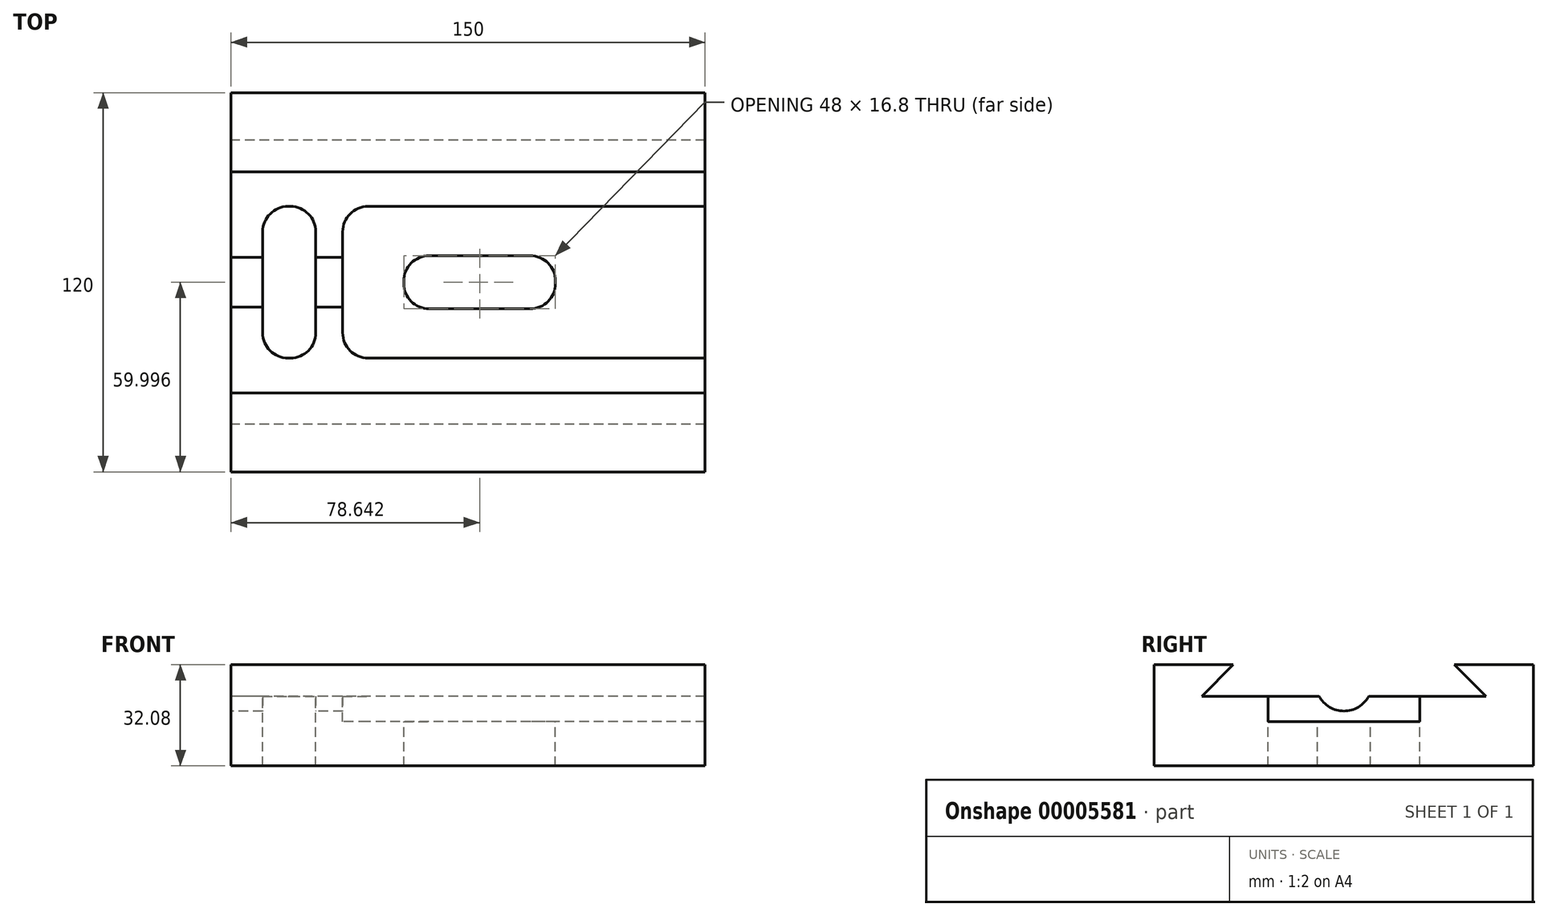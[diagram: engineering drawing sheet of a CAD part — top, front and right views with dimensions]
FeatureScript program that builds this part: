
annotation { "Feature Type Name" : "Feature", "Feature Type Description" : "" }
export const myFeature = defineFeature(function(context is Context, id is Id, definition is map)
    precondition{}
    {
        {
            var Q0;
            Q0=qCreatedBy(makeId("Right.planeOp"),FACE);
            var sketch = newSketch(context, id + "F0", { "sketchPlane" : qUnion([Q0])});
            skLineSegment(sketch, "E0", {"start": v(-27.6, 17.4) * mm, "end": v(-27.6, -14.68) * mm});
            skLineSegment(sketch, "E1", {"start": v(-27.6, -14.68) * mm, "end": v(92.4, -14.68) * mm});
            skLineSegment(sketch, "E2", {"start": v(92.4, -14.68) * mm, "end": v(92.4, 17.4) * mm});
            skLineSegment(sketch, "E3", {"start": v(92.4, 17.4) * mm, "end": v(67.4, 17.4) * mm});
            skLineSegment(sketch, "E4", {"start": v(67.4, 17.4) * mm, "end": v(77.4, 7.4) * mm});
            skLineSegment(sketch, "E5", {"start": v(77.4, 7.4) * mm, "end": v(-12.6, 7.4) * mm});
            skLineSegment(sketch, "E6", {"start": v(-12.6, 7.4) * mm, "end": v(-2.6, 17.4) * mm});
            skLineSegment(sketch, "E7", {"start": v(-2.6, 17.4) * mm, "end": v(-27.6, 17.4) * mm});
            skLineSegment(sketch, "E8", {"start": v(-27.6, 17.4) * mm, "end": v(91, 17.4) * mm, "construction": true});
            skSolve(sketch);
        }
        {
            var Q0;
            Q0=makeQuery(id+"F0.imprint","IMPRINT",FACE,{"disambiguationData":[TD([[makeQuery(id+"F0.imprint","IMPRINT",EDGE,{"derivedFrom":sQuery(id+"F0.wireOp",EDGE,"E0")}),1.0]])]});
            extrude(context, id + "F1", {"entities" : qUnion([Q0]), "depth" : 150 * mm});
        }
        {
            var Q0;
            Q0=makeQuery(id+"F1.opExtrude","SWEPT_FACE",FACE,{"disambiguationData":[OSD([sQuery(id+"F0.wireOp",EDGE,"E5")])]});
            var sketch = newSketch(context, id + "F2", { "sketchPlane" : qUnion([Q0])});
            skLineSegment(sketch, "E9", {"start": v(150, 32.4) * mm, "end": v(0, 32.4) * mm, "construction": true});
            skLineSegment(sketch, "E10.bottom", {"start": v(150, 8.4) * mm, "end": v(43.3, 8.4) * mm, "construction": true});
            skLineSegment(sketch, "E10.top", {"start": v(150, 56.4) * mm, "end": v(43.3, 56.4) * mm, "construction": true});
            skLineSegment(sketch, "E10.left", {"start": v(150, 8.4) * mm, "end": v(150, 56.4) * mm});
            skLineSegment(sketch, "E10.right", {"start": v(35.3, 16.4) * mm, "end": v(35.3, 48.4) * mm, "construction": true});
            skLineSegment(sketch, "E11", {"start": v(35.3, 32.4) * mm, "end": v(150, 32.4) * mm, "construction": true});
            skLineSegment(sketch, "E12.bottom", {"start": v(18, 8.4) * mm, "end": v(18.8, 8.4) * mm});
            skLineSegment(sketch, "E12.top", {"start": v(18, 56.4) * mm, "end": v(18.8, 56.4) * mm});
            skLineSegment(sketch, "E12.left", {"start": v(10, 16.4) * mm, "end": v(10, 48.4) * mm});
            skLineSegment(sketch, "E12.right", {"start": v(26.8, 16.4) * mm, "end": v(26.8, 48.4) * mm});
            skPoint(sketch, "E13.visualSharp", {"position": v(26.8, 8.4) * mm});
            skArc(sketch, "E13.filletArc", {"start": v(18.8, 8.4) * mm, "mid": v(24.46, 10.74) * mm, "end": v(26.8, 16.4) * mm});
            skPoint(sketch, "E14.visualSharp", {"position": v(10, 8.4) * mm});
            skArc(sketch, "E14.filletArc", {"start": v(10, 16.4) * mm, "mid": v(12.34, 10.74) * mm, "end": v(18, 8.4) * mm});
            skPoint(sketch, "E15.visualSharp", {"position": v(10, 56.4) * mm});
            skArc(sketch, "E15.filletArc", {"start": v(18, 56.4) * mm, "mid": v(12.34, 54.05) * mm, "end": v(10, 48.4) * mm});
            skPoint(sketch, "E16.visualSharp", {"position": v(26.8, 56.4) * mm});
            skArc(sketch, "E16.filletArc", {"start": v(26.8, 48.4) * mm, "mid": v(24.46, 54.05) * mm, "end": v(18.8, 56.4) * mm});
            skPoint(sketch, "E17.visualSharp", {"position": v(35.3, 8.4) * mm});
            skArc(sketch, "E17.filletArc", {"start": v(35.3, 16.4) * mm, "mid": v(37.64, 10.74) * mm, "end": v(43.3, 8.4) * mm, "construction": true});
            skPoint(sketch, "E18.visualSharp", {"position": v(35.3, 56.4) * mm});
            skArc(sketch, "E18.filletArc", {"start": v(43.3, 56.4) * mm, "mid": v(37.64, 54.05) * mm, "end": v(35.3, 48.4) * mm, "construction": true});
            skLineSegment(sketch, "E19", {"start": v(63.46, 56.4) * mm, "end": v(63.46, 8.4) * mm, "construction": true});
            skLineSegment(sketch, "E20", {"start": v(18.8, 56.4) * mm, "end": v(18.8, 8.4) * mm, "construction": true});
            skLineSegment(sketch, "E21", {"start": v(10, 32.4) * mm, "end": v(26.8, 32.4) * mm, "construction": true});
            skSolve(sketch);
        }
        {
            var Q0;
            Q0=makeQuery(id+"F2.imprint","IMPRINT",FACE,{"disambiguationData":[TD([[makeQuery(id+"F2.imprint","IMPRINT",EDGE,{"derivedFrom":sQuery(id+"F2.wireOp",EDGE,"E12.bottom")}),1.0]])]});
            var Q1;
            Q1=makeQuery(id+"F1.opExtrude","SWEPT_FACE",FACE,{"disambiguationData":[OSD([sQuery(id+"F0.wireOp",EDGE,"E1")])]});
            extrude(context, id + "F3", {"entities" : qUnion([Q0]), "operationType" : NewBodyOperationType.REMOVE, "endBound" : BoundingType.UP_TO_SURFACE, "oppositeDirection" : true, "endBoundEntityFace" : qUnion([Q1]), "depth" : 17.3 * mm});
        }
        {
            var Q0;
            Q0=makeQuery(id+"F1.opExtrude","SWEPT_FACE",FACE,{"disambiguationData":[OSD([sQuery(id+"F0.wireOp",EDGE,"E5")])]});
            var sketch = newSketch(context, id + "F4", { "sketchPlane" : qUnion([Q0])});
            skLineSegment(sketch, "E22", {"start": v(150, 8.4) * mm, "end": v(43.3, 8.4) * mm});
            skLineSegment(sketch, "E23", {"start": v(35.3, 16.4) * mm, "end": v(35.3, 48.4) * mm});
            skLineSegment(sketch, "E24", {"start": v(43.3, 56.4) * mm, "end": v(150, 56.4) * mm});
            skLineSegment(sketch, "E25", {"start": v(150, 56.4) * mm, "end": v(150, 8.4) * mm});
            skPoint(sketch, "E26.visualSharp", {"position": v(35.3, 8.4) * mm});
            skArc(sketch, "E26.filletArc", {"start": v(35.3, 16.4) * mm, "mid": v(37.64, 10.74) * mm, "end": v(43.3, 8.4) * mm});
            skPoint(sketch, "E27.visualSharp", {"position": v(35.3, 56.4) * mm});
            skArc(sketch, "E27.filletArc", {"start": v(43.3, 56.4) * mm, "mid": v(37.64, 54.05) * mm, "end": v(35.3, 48.4) * mm});
            skSolve(sketch);
        }
        {
            var Q0;
            Q0=makeQuery(id+"F4.imprint","IMPRINT",FACE,{"disambiguationData":[TD([[makeQuery(id+"F4.imprint","IMPRINT",EDGE,{"derivedFrom":sQuery(id+"F4.wireOp",EDGE,"E22")}),-1.0]])]});
            extrude(context, id + "F5", {"entities" : qUnion([Q0]), "operationType" : NewBodyOperationType.REMOVE, "oppositeDirection" : true, "depth" : 8.1 * mm});
        }
        {
            var Q0;
            Q0=makeQuery(id+"F5.boolean.opBoolean","COPY",FACE,{"derivedFrom":makeQuery(id+"F5.opExtrude","CAP_FACE",FACE,{"disambiguationData":[OSD([sQuery(id+"F4.wireOp",EDGE,"E22"),sQuery(id+"F4.wireOp",EDGE,"E23"),sQuery(id+"F4.wireOp",EDGE,"E24"),sQuery(id+"F4.wireOp",EDGE,"E25"),sQuery(id+"F4.wireOp",EDGE,"E26.filletArc"),sQuery(id+"F4.wireOp",EDGE,"E27.filletArc")])],"isStart":false})});
            var sketch = newSketch(context, id + "F6", { "sketchPlane" : qUnion([Q0])});
            skLineSegment(sketch, "E28.bottom", {"start": v(94.64, 24) * mm, "end": v(62.64, 24) * mm});
            skLineSegment(sketch, "E28.top", {"start": v(94.64, 40.8) * mm, "end": v(62.64, 40.8) * mm});
            skLineSegment(sketch, "E28.left", {"start": v(102.64, 32) * mm, "end": v(102.64, 32.8) * mm});
            skLineSegment(sketch, "E28.right", {"start": v(54.64, 32) * mm, "end": v(54.64, 32.8) * mm});
            skLineSegment(sketch, "E29", {"start": v(102.64, 32.4) * mm, "end": v(54.64, 32.4) * mm, "construction": true});
            skPoint(sketch, "E30.visualSharp", {"position": v(102.64, 24) * mm});
            skArc(sketch, "E30.filletArc", {"start": v(94.64, 24) * mm, "mid": v(100.3, 26.34) * mm, "end": v(102.64, 32) * mm});
            skPoint(sketch, "E31.visualSharp", {"position": v(54.64, 24) * mm});
            skArc(sketch, "E31.filletArc", {"start": v(54.64, 32) * mm, "mid": v(56.99, 26.34) * mm, "end": v(62.64, 24) * mm});
            skPoint(sketch, "E32.visualSharp", {"position": v(54.64, 40.8) * mm});
            skArc(sketch, "E32.filletArc", {"start": v(62.64, 40.8) * mm, "mid": v(56.99, 38.45) * mm, "end": v(54.64, 32.8) * mm});
            skPoint(sketch, "E33.visualSharp", {"position": v(102.64, 40.8) * mm});
            skArc(sketch, "E33.filletArc", {"start": v(102.64, 32.8) * mm, "mid": v(100.3, 38.45) * mm, "end": v(94.64, 40.8) * mm});
            skSolve(sketch);
        }
        {
            var Q0;
            Q0=makeQuery(id+"F6.imprint","IMPRINT",FACE,{"disambiguationData":[TD([[makeQuery(id+"F6.imprint","IMPRINT",EDGE,{"derivedFrom":sQuery(id+"F6.wireOp",EDGE,"E28.bottom")}),-1.0]])]});
            extrude(context, id + "F7", {"entities" : qUnion([Q0]), "operationType" : NewBodyOperationType.REMOVE, "oppositeDirection" : true, "depth" : 26 * mm});
        }
        {
            var Q0;
            Q0=makeQuery(id+"F1.opExtrude","CAP_FACE",FACE,{"disambiguationData":[OSD([sQuery(id+"F0.wireOp",EDGE,"E0"),sQuery(id+"F0.wireOp",EDGE,"E1"),sQuery(id+"F0.wireOp",EDGE,"E2"),sQuery(id+"F0.wireOp",EDGE,"E3"),sQuery(id+"F0.wireOp",EDGE,"E4"),sQuery(id+"F0.wireOp",EDGE,"E5"),sQuery(id+"F0.wireOp",EDGE,"E6"),sQuery(id+"F0.wireOp",EDGE,"E7")])],"isStart":true});
            var sketch = newSketch(context, id + "F8", { "sketchPlane" : qUnion([Q0])});
            skLineSegment(sketch, "E34", {"start": v(-32.4, 7.4) * mm, "end": v(-32.4, 11.6) * mm, "construction": true});
            skCircle(sketch, "E35", {"center": v(-32.4, 11.6) * mm, "radius": 8.9 * mm});
            skSolve(sketch);
        }
        {
            var Q0;
            {var subQ0=makeQuery(id+"F1.opExtrude","CAP_EDGE",EDGE,{"disambiguationData":[OSD([sQuery(id+"F0.wireOp",EDGE,"E5")])],"isStart":true});var subQ1=sQuery(id+"F8.wireOp",EDGE,"E35");var subQ3=makeQuery(id+"F8.imprint","INTERSECT",VERTEX,{"disambiguationData":[OD(0.0)],"derivedFrom":[subQ0,subQ1]});Q0=qUnion([makeQuery(id+"F8.imprint","IMPRINT",FACE,{"disambiguationData":[TD([[makeQuery(id+"F8.imprint","IMPRINT",EDGE,{"disambiguationData":[TD([[subQ3,1.0]])],"derivedFrom":subQ1}),1.0]])]}),makeQuery(id+"F8.imprint","IMPRINT",FACE,{"disambiguationData":[TD([[makeQuery(id+"F8.imprint","IMPRINT",EDGE,{"disambiguationData":[TD([[subQ3,-1.0]])],"derivedFrom":subQ1}),1.0]])]})]);}
            var Q1;
            Q1=makeQuery(id+"F5.boolean.opBoolean","COPY",FACE,{"derivedFrom":makeQuery(id+"F5.opExtrude","SWEPT_FACE",FACE,{"disambiguationData":[OSD([sQuery(id+"F4.wireOp",EDGE,"E23")])]})});
            extrude(context, id + "F9", {"entities" : qUnion([Q0]), "operationType" : NewBodyOperationType.REMOVE, "endBound" : BoundingType.UP_TO_SURFACE, "oppositeDirection" : true, "endBoundEntityFace" : qUnion([Q1]), "depth" : 25 * mm});
        }
        {
            var Q0;
            Q0=makeQuery(id+"F5.boolean.opBoolean","COPY",FACE,{"derivedFrom":makeQuery(id+"F5.opExtrude","SWEPT_FACE",FACE,{"disambiguationData":[OSD([sQuery(id+"F4.wireOp",EDGE,"E23")])]})});
            var sketch = newSketch(context, id + "F10", { "sketchPlane" : qUnion([Q0])});
            skLineSegment(sketch, "E36", {"start": v(32.4, 7.4) * mm, "end": v(32.4, 11.6) * mm, "construction": true});
            skSolve(sketch);
        }
    });
